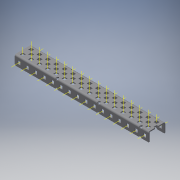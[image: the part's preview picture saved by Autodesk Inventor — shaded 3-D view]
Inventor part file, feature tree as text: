
AUTODESK INVENTOR PART (.ipt)
format: ipt  version: 2017 SP1 (Build 210196100, 196)  size: 2,027,008 bytes
history: native  units: in
note: dims shown in document units (in); Inventor stores cm internally (conversion verified against a paired STEP export)
features: other x86, pattern_linear x3, sheet_metal_op x1, extrude x1, imported_body x1, sketch x1
ambient origin geometry x8: Origin, YZ Plane, XZ Plane, XY Plane, X Axis, Y Axis, Z Axis, Center Point
bodies: Body1 (feature_tree)
feature tree (93):
  sheet_metal_op  "Fold1"
  other  "C-Channel"
  extrude  "length cut"  Depth=0.5in
  other  "top axis"
  other  "inner axis"
  other  "front axis"
  other  "back axis"
  pattern_linear  "top axes"  Spacing1=0.5in  [1 undecoded]
  pattern_linear  "inner axes"  Spacing1=0.5in  [1 undecoded]
  pattern_linear  "horiz axes"  Spacing1=-8.0in  [1 undecoded]
  other  "right plane"
  imported_body  "Base1"
  sketch  "Sketch1"  dims[d1=0.0in d4=0.5in d5=0.7874in d7=0.5in d10=0.5in d13=0.5in d14=-8.0in d15=0.0in d16=0.0in d17=0.0in d18=0.0in d19=0.0in]
  other  "Work Point1"
  other  "Work Point2"
  other  "Work Point3"
  other  "Work Point4"
  other  "Work Axis5"
  other  "Work Axis6"
  other  "Work Axis7"
  other  "Work Axis8"
  other  "Work Axis11"
  other  "Work Axis12"
  other  "Work Axis13"
  other  "Work Axis14"
  other  "Work Axis15"
  other  "Work Axis18"
  other  "Work Axis19"
  other  "Work Axis20"
  other  "Work Axis23"
  other  "Work Axis24"
  other  "Work Axis25"
  other  "Work Axis26"
  other  "Work Axis30"
  other  "Work Axis31"
  other  "Work Axis32"
  other  "Work Axis33"
  other  "left plane"
  other  "Work Axis37"
  other  "Work Axis38"
  other  "Work Axis39"
  other  "Work Axis40"
  other  "Work Axis41"
  other  "Work Axis42"
  other  "Work Axis43"
  other  "Work Axis44"
  other  "Work Axis45"
  other  "Work Axis46"
  other  "Work Axis57"
  other  "Work Axis58"
  other  "Work Axis59"
  other  "Work Axis60"
  other  "Work Axis61"
  other  "Work Axis62"
  other  "Work Axis63"
  other  "Work Axis64"
  other  "Work Axis65"
  other  "Work Axis66"
  other  "Work Axis77"
  other  "Work Axis78"
  other  "Work Axis79"
  other  "Work Axis80"
  other  "Work Axis81"
  other  "Work Axis82"
  other  "Work Axis83"
  other  "Work Axis84"
  other  "Work Axis85"
  other  "Work Axis86"
  other  "Work Axis97"
  other  "Work Axis98"
  other  "Work Axis99"
  other  "Work Axis100"
  other  "Work Axis101"
  other  "Work Axis102"
  other  "Work Axis103"
  other  "Work Axis104"
  other  "Work Axis105"
  other  "Work Axis106"
  other  "Work Axis117"
  other  "Work Axis118"
  other  "Work Axis119"
  other  "Work Axis120"
  other  "Work Axis121"
  other  "Work Axis122"
  other  "Work Axis123"
  other  "Work Axis124"
  other  "Work Axis125"
  other  "Work Axis126"
  other  "Work Axis137"
  other  "Work Axis138"
  other  "Work Axis139"
  other  "Work Axis140"
  other  "Work Axis141"
note: 3 required parameter values undecoded (feature->parameter linkage not recoverable at this tier; creation-order binding heuristic only, values carry confidence <= 0.55)
